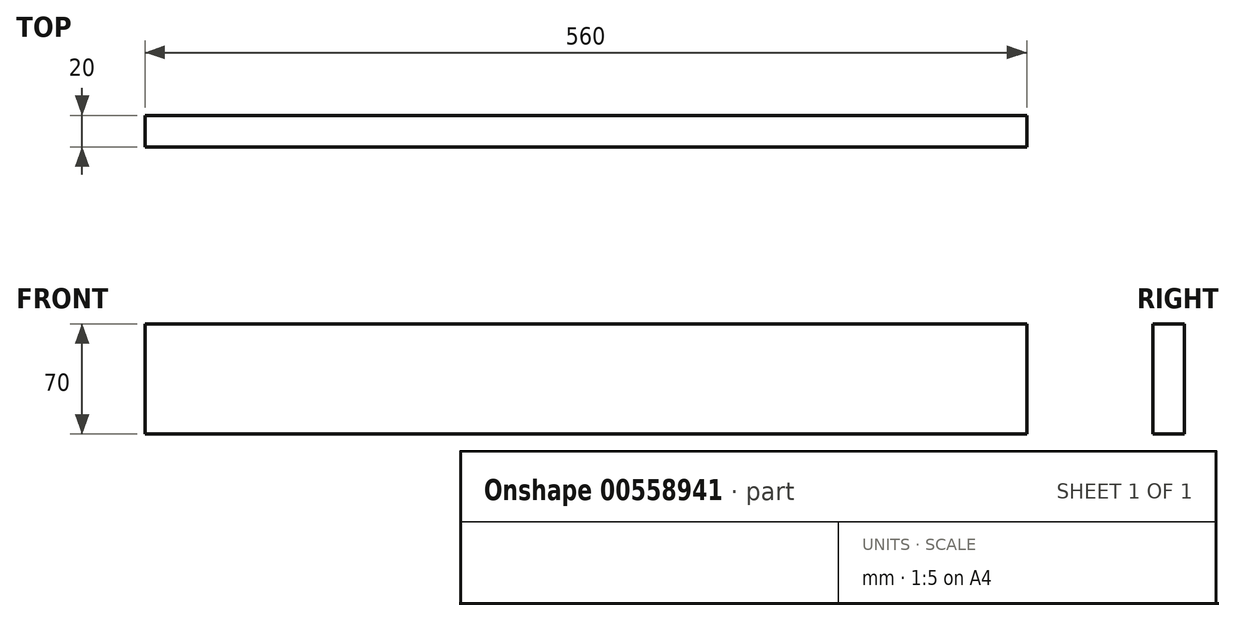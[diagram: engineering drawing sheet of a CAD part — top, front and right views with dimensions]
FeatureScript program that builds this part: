
annotation { "Feature Type Name" : "Feature", "Feature Type Description" : "" }
export const myFeature = defineFeature(function(context is Context, id is Id, definition is map)
    precondition{}
    {
        {
            var Q0;
            Q0=qCreatedBy(makeId("Front.planeOp"),FACE);
            var sketch = newSketch(context, id + "F0", { "sketchPlane" : qUnion([Q0])});
            skLineSegment(sketch, "E0.bottom", {"start": v(280, -35) * mm, "end": v(-280, -35) * mm});
            skLineSegment(sketch, "E0.top", {"start": v(280, 35) * mm, "end": v(-280, 35) * mm});
            skLineSegment(sketch, "E0.left", {"start": v(280, -35) * mm, "end": v(280, 35) * mm});
            skLineSegment(sketch, "E0.right", {"start": v(-280, -35) * mm, "end": v(-280, 35) * mm});
            skPoint(sketch, "E0.middle", {"position": v(0, 0) * mm});
            skSolve(sketch);
        }
        {
            var Q0;
            Q0=makeQuery(id+"F0.imprint","IMPRINT",FACE,{"disambiguationData":[TD([[makeQuery(id+"F0.imprint","IMPRINT",EDGE,{"derivedFrom":sQuery(id+"F0.wireOp",EDGE,"E0.bottom")}),-1.0]])]});
            extrude(context, id + "F1", {"entities" : qUnion([Q0]), "depth" : 20 * mm, "offsetDistance" : 25 * mm});
        }
    });
